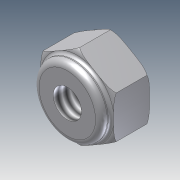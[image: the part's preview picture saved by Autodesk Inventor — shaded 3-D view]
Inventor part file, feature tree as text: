
AUTODESK INVENTOR PART (.ipt)
format: ipt  version: 2012 (Build 160160000, 160)  size: 178,176 bytes
history: native  units: in
note: dims shown in document units (in); Inventor stores cm internally (conversion verified against a paired STEP export)
features: sketch x3, extrude x2, fillet x2, plane x1, revolve x1, hole x1, projected_geometry x1
ambient origin geometry x8: Origin, YZ Plane, XZ Plane, XY Plane, X Axis, Y Axis, Z Axis, Center Point
bodies: Solid1 (feature_tree)
feature tree (11):
  extrude  "Extrusion1"  Depth=0.1844in TaperAngle=0.0deg
  plane  "Work Plane1"
  revolve  "Revolution1"  [1 undecoded]
  extrude  "Extrusion2"  TaperAngle=90.0deg  [1 undecoded]
  fillet  "Fillet1"  Radius=0.35in
  fillet  "Fillet2"  Radius=0.05in
  hole  "Hole1"  [1 undecoded]
  sketch  "Sketch1"  dims[d0=0.375in d1=0.1844in d2=0.0in]
  sketch  "Sketch3"  dims[d4=0.04in d5=0.03in]
  sketch  "Sketch4"  dims[d6=0.03in d7=90.0deg d8=0.35in d9=0.05in d10=0.0in d11=0.03in d12=0.015in d13=1.0in d14=1.0in d15=0.145in d16=0.5in d17=0.375in d18=0.25in d19=0.5635in d20=0.75in d21=0.8108in]
  projected_geometry  "Project Cut Edges1"
note: 3 required parameter values undecoded (feature->parameter linkage not recoverable at this tier; creation-order binding heuristic only, values carry confidence <= 0.55)